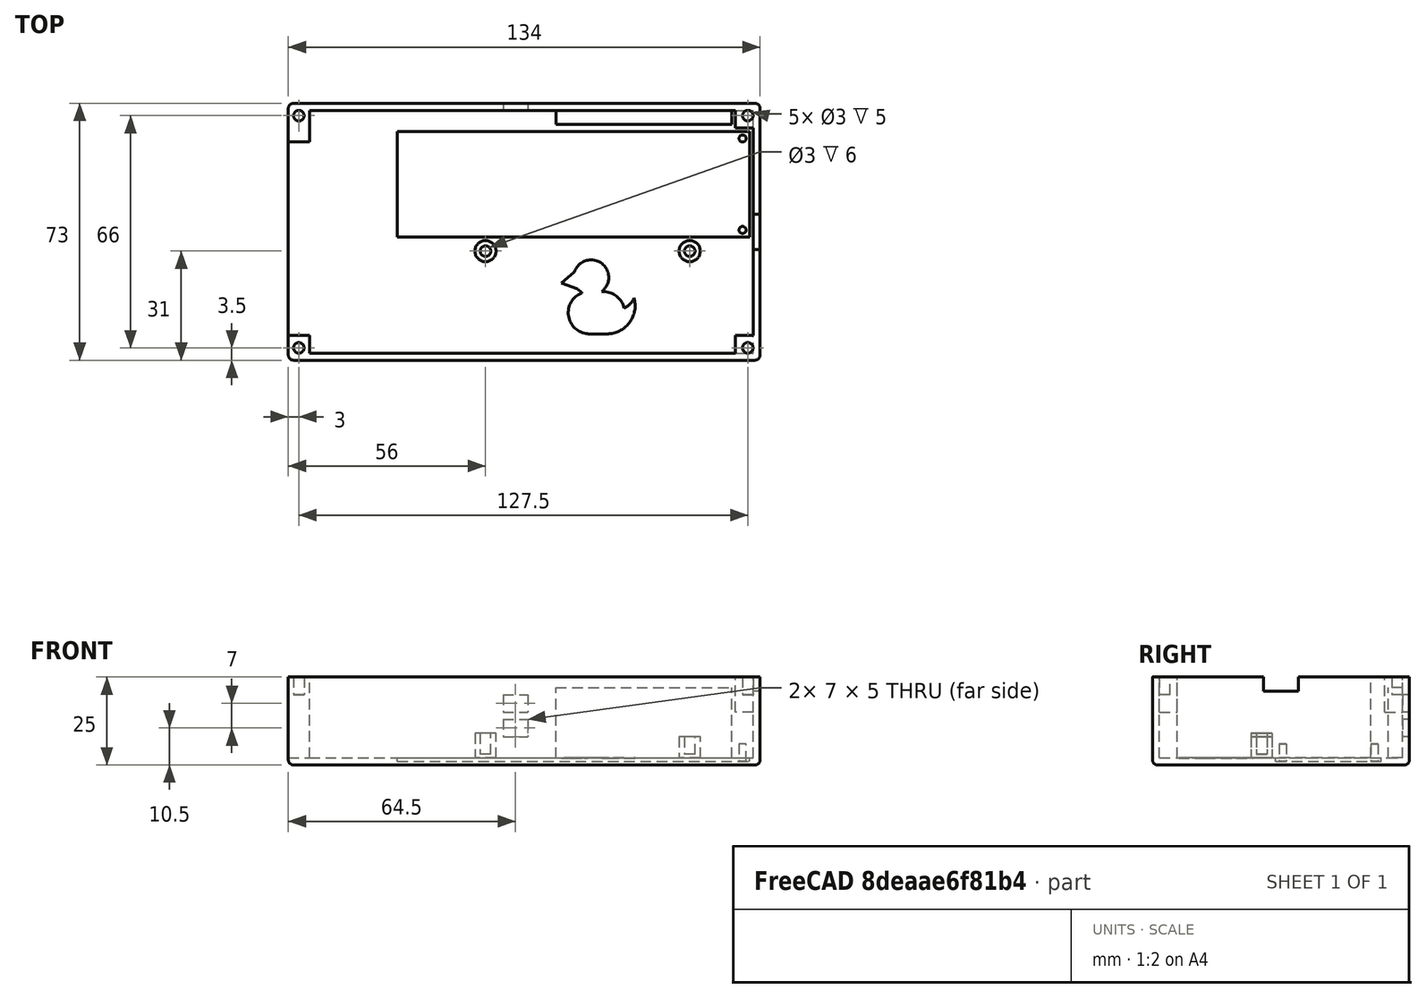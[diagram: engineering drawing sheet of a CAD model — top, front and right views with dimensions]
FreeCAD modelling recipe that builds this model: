
FCSTD DOCUMENT  (FreeCAD 1.0R39285 (Git))
Label: caseBottom
License: All rights reserved
LicenseURL: https://en.wikipedia.org/wiki/All_rights_reserved
objects: PartDesign::SubtractiveCylinder×12, PartDesign::SubtractiveBox×7, PartDesign::AdditiveCylinder×5, PartDesign::AdditiveBox×4, PartDesign::Fillet×4, PartDesign::SubtractivePrism×1, PartDesign::Body×1
note: 100 computed .brp shape members not serialized (recipe doc carries the construction recipe); baked Part::Feature solids carry a one-line shape summary decoded from their .brp

FEATURE [PartDesign::AdditiveBox] Box  label="base"
  AttacherType = Attacher::AttachEngine3D
  Height = 25
  Length = 134
  Refine = true
  Suppressed = false
  Width = 73
FEATURE [PartDesign::SubtractiveBox] Box001  label="primaryHollow"
  AttacherType = Attacher::AttachEngine3D
  AttachmentOffset = pos=(6,2,-23) rot=(0,0,1;0rad)
  AttachmentSupport = -> [Box]
  BaseFeature = -> Box
  Height = 23
  Length = 126
  MapMode = 5
  Placement = pos=(6,2,2) rot=(0,0,1;0rad)
  Refine = true
  Suppressed = false
  Width = 69
FEATURE [PartDesign::SubtractiveBox] Box002  label="dacGap"
  AttacherType = Attacher::AttachEngine3D
  AttachmentOffset = pos=(-8,5,0) rot=(0,0,1;0rad)
  AttachmentSupport = -> [Box001]
  BaseFeature = -> Box001
  Height = 23
  Length = 10
  MapMode = 2
  Placement = pos=(-2,7,2) rot=(0,0,1;0rad)
  Refine = true
  Suppressed = false
  Width = 55
FEATURE [PartDesign::SubtractiveBox] Box003  label="batteryPCBRecess"
  AttacherType = Attacher::AttachEngine3D
  AttachmentOffset = pos=(33,28,-1) rot=(0,0,1;0rad)
  AttachmentSupport = -> [Box002]
  BaseFeature = -> Box002
  Height = 1
  Length = 100
  MapMode = 5
  Placement = pos=(31,35,1) rot=(0,0,1;0rad)
  Refine = true
  Suppressed = false
  Width = 30
FEATURE [PartDesign::AdditiveCylinder] Cylinder  label="batteryPCBSupport1"
  Angle = 360
  AttacherType = Attacher::AttachEngine3D
  AttachmentOffset = pos=(98,2,0) rot=(0,0,1;0rad)
  AttachmentSupport = -> [Box003]
  BaseFeature = -> Box003
  FirstAngle = 0
  Height = 5
  MapMode = 5
  Placement = pos=(129,37,1) rot=(0,0,1;0rad)
  Radius = 1
  Refine = true
  SecondAngle = 0
  Suppressed = false
FEATURE [PartDesign::AdditiveCylinder] Cylinder001  label="batteryPCBSupport2"
  Angle = 360
  AttacherType = Attacher::AttachEngine3D
  AttachmentOffset = pos=(98,28,0) rot=(0,0,1;0rad)
  AttachmentSupport = -> [Box003]
  BaseFeature = -> Cylinder
  FirstAngle = 0
  Height = 5
  MapMode = 2
  Placement = pos=(129,63,1) rot=(0,0,1;0rad)
  Radius = 1
  Refine = true
  SecondAngle = 0
  Suppressed = false
FEATURE [PartDesign::AdditiveCylinder] Cylinder002  label="rpiSupport1"
  Angle = 360
  AttacherType = Attacher::AttachEngine3D
  AttachmentOffset = pos=(-15,-32,-1) rot=(0,0,1;0rad)
  AttachmentSupport = -> [Cylinder001]
  BaseFeature = -> Cylinder001
  FirstAngle = 0
  Height = 7
  MapMode = 5
  Placement = pos=(114,31,1) rot=(0,0,1;0rad)
  Radius = 3
  Refine = true
  SecondAngle = 0
  Suppressed = false
FEATURE [PartDesign::SubtractiveCylinder] Cylinder003  label="rpiSupport1Hollow"
  Angle = 360
  AttacherType = Attacher::AttachEngine3D
  AttachmentOffset = pos=(0,0,1) rot=(0,0,1;0rad)
  AttachmentSupport = -> [Cylinder002]
  BaseFeature = -> Cylinder002
  FirstAngle = 0
  Height = 6
  MapMode = 5
  Placement = pos=(114,31,3) rot=(0,0,1;0rad)
  Radius = 1.5
  Refine = true
  SecondAngle = 0
  Suppressed = false
FEATURE [PartDesign::AdditiveCylinder] Cylinder004  label="rpiSupport2"
  Angle = 360
  AttacherType = Attacher::AttachEngine3D
  AttachmentOffset = pos=(-58,0,0) rot=(0,0,1;0rad)
  AttachmentSupport = -> [Cylinder003]
  BaseFeature = -> Cylinder003
  FirstAngle = 0
  Height = 7
  MapMode = 5
  Placement = pos=(56,31,2) rot=(0,0,1;0rad)
  Radius = 3
  Refine = true
  SecondAngle = 0
  Suppressed = false
FEATURE [PartDesign::SubtractiveCylinder] Cylinder005  label="rpiSupport2Hollow"
  Angle = 360
  AttacherType = Attacher::AttachEngine3D
  AttachmentOffset = pos=(0,0,-6) rot=(0,0,1;0rad)
  AttachmentSupport = -> [Cylinder004]
  BaseFeature = -> Cylinder004
  FirstAngle = 0
  Height = 6
  MapMode = 5
  Placement = pos=(56,31,3) rot=(0,0,1;0rad)
  Radius = 1.5
  Refine = true
  SecondAngle = 0
  Suppressed = false
FEATURE [PartDesign::SubtractiveBox] Box004  label="powerSwitch"
  AttacherType = Attacher::AttachEngine3D
  AttachmentOffset = pos=(5,5,-3) rot=(0,0,1;0rad)
  AttachmentSupport = -> [Cylinder005]
  BaseFeature = -> Cylinder005
  Height = 7
  Length = 7
  MapMode = 5
  Placement = pos=(61,74,8) rot=(1,0,0;1.5708rad)
  Refine = true
  Suppressed = false
  Width = 5
FEATURE [PartDesign::SubtractiveBox] Box005  label="holdSwitch"
  AttacherType = Attacher::AttachEngine3D
  AttachmentOffset = pos=(0,7,-3) rot=(0,0,1;0rad)
  AttachmentSupport = -> [Box004]
  BaseFeature = -> Box004
  Height = 5
  Length = 7
  MapMode = 5
  Placement = pos=(61,74,15) rot=(1,0,0;1.5708rad)
  Refine = true
  Suppressed = false
  Width = 5
FEATURE [PartDesign::AdditiveBox] Box006  label="clickwheelSideSupport"
  AttacherType = Attacher::AttachEngine3D
  AttachmentOffset = pos=(15,-13,0) rot=(0,0,1;0rad)
  AttachmentSupport = -> [Box005]
  BaseFeature = -> Box005
  Height = 4
  Length = 50
  MapMode = 5
  Placement = pos=(76,71,2) rot=(1,0,0;1.5708rad)
  Refine = true
  Suppressed = false
  Width = 20
FEATURE [PartDesign::SubtractiveBox] Box007  label="usbPortHollow"
  AttacherType = Attacher::AttachEngine3D
  AttachmentOffset = pos=(-23,29.5,-2) rot=(0,0,1;0rad)
  AttachmentSupport = -> [Box006]
  BaseFeature = -> Box006
  Height = 2
  Length = 4
  MapMode = 5
  Placement = pos=(134,41.5,25) rot=(0.707107,0,-0.707107;3.14159rad)
  Refine = true
  Suppressed = false
  Width = 10
FEATURE [PartDesign::SubtractiveCylinder] Cylinder006  label="topScrewHollow1"
  Angle = 360
  AttacherType = Attacher::AttachEngine3D
  AttachmentOffset = pos=(-38,131,-5) rot=(0,0,1;0rad)
  AttachmentSupport = -> [Box007]
  BaseFeature = -> Box007
  FirstAngle = 0
  Height = 5
  MapMode = 5
  Placement = pos=(3,3.5,20) rot=(0,0,1;1.5708rad)
  Radius = 1.5
  Refine = true
  SecondAngle = 0
  Suppressed = false
FEATURE [PartDesign::SubtractiveCylinder] Cylinder007  label="topScrewHollow2"
  Angle = 360
  AttacherType = Attacher::AttachEngine3D
  AttachmentOffset = pos=(66,0,-5) rot=(0,0,1;0rad)
  AttachmentSupport = -> [Cylinder006]
  BaseFeature = -> Cylinder006
  FirstAngle = 0
  Height = 5
  MapMode = 5
  Placement = pos=(3,69.5,20) rot=(0,0,1;1.5708rad)
  Radius = 1.5
  Refine = true
  SecondAngle = 0
  Suppressed = false
FEATURE [PartDesign::AdditiveBox] Box008  label="bottomScrew1"
  AttacherType = Attacher::AttachEngine3D
  AttachmentOffset = pos=(-67.5,-129,-10) rot=(0,0,1;0rad)
  AttachmentSupport = -> [Cylinder007]
  BaseFeature = -> Cylinder007
  Height = 10
  Length = 5
  MapMode = 5
  Placement = pos=(132,2,15) rot=(0,0,1;1.5708rad)
  Refine = true
  Suppressed = false
  Width = 5
FEATURE [PartDesign::AdditiveBox] Box009  label="bottomScrew2"
  AttacherType = Attacher::AttachEngine3D
  AttachmentOffset = pos=(64,0,-10) rot=(0,0,1;0rad)
  AttachmentSupport = -> [Box008]
  BaseFeature = -> Box008
  Height = 10
  Length = 5
  MapMode = 5
  Placement = pos=(132,66,15) rot=(0,0,1;1.5708rad)
  Refine = true
  Suppressed = false
  Width = 5
FEATURE [PartDesign::SubtractiveCylinder] Cylinder008  label="bottomScrewHollow2"
  Angle = 360
  AttacherType = Attacher::AttachEngine3D
  AttachmentOffset = pos=(3.5,1.5,-5) rot=(0,0,1;0rad)
  AttachmentSupport = -> [Box009]
  BaseFeature = -> Box009
  FirstAngle = 0
  Height = 5
  MapMode = 5
  Placement = pos=(130.5,69.5,20) rot=(0,0,1;1.5708rad)
  Radius = 1.5
  Refine = true
  SecondAngle = 0
  Suppressed = false
FEATURE [PartDesign::SubtractiveCylinder] Cylinder009  label="BottomScrewHollow1"
  Angle = 360
  AttacherType = Attacher::AttachEngine3D
  AttachmentOffset = pos=(-66,0,-5) rot=(0,0,1;0rad)
  AttachmentSupport = -> [Cylinder008]
  BaseFeature = -> Cylinder008
  FirstAngle = 0
  Height = 5
  MapMode = 5
  Placement = pos=(130.5,3.5,20) rot=(0,0,1;1.5708rad)
  Radius = 1.5
  Refine = true
  SecondAngle = 0
  Suppressed = false
FEATURE [PartDesign::Fillet] Fillet
  Base = -> Cylinder009 [Edge62]
  BaseFeature = -> Cylinder009
  Placement = pos=(130.5,3.5,20) rot=(0,0,1;1.5708rad)
  Radius = 1.5
  Refine = true
  SupportTransform = false
  Suppressed = false
  UseAllEdges = false
FEATURE [PartDesign::Fillet] Fillet001
  Base = -> Fillet [Edge14]
  BaseFeature = -> Fillet
  Placement = pos=(130.5,3.5,20) rot=(0,0,1;1.5708rad)
  Radius = 1.5
  Refine = true
  SupportTransform = false
  Suppressed = false
  UseAllEdges = false
FEATURE [PartDesign::Fillet] Fillet002
  Base = -> Fillet001 [Edge31]
  BaseFeature = -> Fillet001
  Placement = pos=(130.5,3.5,20) rot=(0,0,1;1.5708rad)
  Radius = 1.5
  Refine = true
  SupportTransform = false
  Suppressed = false
  UseAllEdges = false
FEATURE [PartDesign::Fillet] Fillet003
  Base = -> Fillet002 [Edge1]
  BaseFeature = -> Fillet002
  Placement = pos=(130.5,3.5,20) rot=(0,0,1;1.5708rad)
  Radius = 1.5
  Refine = true
  SupportTransform = false
  Suppressed = false
  UseAllEdges = false
FEATURE [PartDesign::SubtractiveCylinder] Cylinder010
  Angle = 360
  AttacherType = Attacher::AttachEngine3D
  AttachmentOffset = pos=(10,40,-0.1) rot=(0,0,1;0rad)
  AttachmentSupport = -> [Fillet003]
  BaseFeature = -> Fillet003
  FirstAngle = 0
  Height = 0.1
  MapMode = 5
  Placement = pos=(90.5,13.5,1.9) rot=(0,0,1;1.5708rad)
  Radius = 6
  Refine = true
  SecondAngle = 0
  Suppressed = false
FEATURE [PartDesign::SubtractiveCylinder] Cylinder011
  Angle = 360
  AttacherType = Attacher::AttachEngine3D
  AttachmentOffset = pos=(0,5,-0.1) rot=(0,0,1;0rad)
  AttachmentSupport = -> [Cylinder010]
  BaseFeature = -> Cylinder010
  FirstAngle = 0
  Height = 0.1
  MapMode = 5
  Placement = pos=(85.5,13.5,1.9) rot=(0,0,1;1.5708rad)
  Radius = 6
  Refine = true
  SecondAngle = 0
  Suppressed = false
FEATURE [PartDesign::SubtractiveBox] Box010
  AttacherType = Attacher::AttachEngine3D
  AttachmentOffset = pos=(-6,-5.5,-0.1) rot=(0,0,1;0rad)
  AttachmentSupport = -> [Cylinder011]
  BaseFeature = -> Cylinder011
  Height = 0.1
  Length = 12
  MapMode = 5
  Placement = pos=(91,7.5,1.9) rot=(0,0,1;1.5708rad)
  Refine = true
  Suppressed = false
  Width = 6
FEATURE [PartDesign::SubtractiveCylinder] Cylinder012
  Angle = 360
  AttacherType = Attacher::AttachEngine3D
  AttachmentOffset = pos=(16,5,-0.1) rot=(0,0,1;0rad)
  AttachmentSupport = -> [Box010]
  BaseFeature = -> Box010
  FirstAngle = 0
  Height = 0.1
  MapMode = 5
  Placement = pos=(86,23.5,1.9) rot=(0,0,1;1.5708rad)
  Radius = 5
  Refine = true
  SecondAngle = 0
  Suppressed = false
FEATURE [PartDesign::SubtractiveCylinder] Cylinder013
  Angle = 360
  AttacherType = Attacher::AttachEngine3D
  AttachmentOffset = pos=(-8,-4.5,-0.1) rot=(0,0,1;0rad)
  AttachmentSupport = -> [Cylinder012]
  BaseFeature = -> Cylinder012
  FirstAngle = 0
  Height = 0.1
  MapMode = 5
  Placement = pos=(90.5,15.5,1.9) rot=(0,0,1;1.5708rad)
  Radius = 8
  Refine = true
  SecondAngle = 0
  Suppressed = false
FEATURE [PartDesign::AdditiveCylinder] Cylinder014
  Angle = 360
  AttacherType = Attacher::AttachEngine3D
  AttachmentOffset = pos=(4,-3,-0.1) rot=(0,0,1;0rad)
  AttachmentSupport = -> [Cylinder013]
  BaseFeature = -> Cylinder013
  FirstAngle = 0
  Height = 0.1
  MapMode = 5
  Placement = pos=(93.5,19.5,1.9) rot=(0,0,1;1.5708rad)
  Radius = 5
  Refine = true
  SecondAngle = 0
  Suppressed = false
FEATURE [PartDesign::SubtractiveCylinder] Cylinder015
  Angle = 360
  AttacherType = Attacher::AttachEngine3D
  AttachmentOffset = pos=(-6,4,-0.1) rot=(0,0,1;0rad)
  AttachmentSupport = -> [Cylinder014]
  BaseFeature = -> Cylinder014
  FirstAngle = 0
  Height = 0.1
  MapMode = 5
  Placement = pos=(89.5,13.5,1.9) rot=(0,0,1;1.5708rad)
  Radius = 6
  Refine = true
  SecondAngle = 0
  Suppressed = false
FEATURE [PartDesign::SubtractiveCylinder] Cylinder016
  Angle = 360
  AttacherType = Attacher::AttachEngine3D
  AttachmentOffset = pos=(10,3.5,-0.1) rot=(0,0,1;0rad)
  AttachmentSupport = -> [Cylinder015]
  BaseFeature = -> Cylinder015
  FirstAngle = 0
  Height = 0.1
  MapMode = 5
  Placement = pos=(86,23.5,1.9) rot=(0,0,1;1.5708rad)
  Radius = 5
  Refine = true
  SecondAngle = 0
  Suppressed = false
FEATURE [PartDesign::SubtractivePrism] Prism
  AttacherType = Attacher::AttachEngine3D
  AttachmentOffset = pos=(-1,5.5,-0.1) rot=(0,0,-1;0.349066rad)
  AttachmentSupport = -> [Cylinder016]
  BaseFeature = -> Cylinder016
  Circumradius = 3
  FirstAngle = 0
  Height = 0.1
  MapMode = 5
  Placement = pos=(80.5,22.5,1.9) rot=(0,0,1;1.22173rad)
  Polygon = 3
  Refine = true
  SecondAngle = 0
  Suppressed = false
FEATURE [PartDesign::Body] Body
  AllowCompound = false
  Group = -> [Box,Box001,Box002,Box003,Cylinder,Cylinder001,Cylinder002,Cylinder003,Cylinder004,Cylinder005,Box004,Box005,Box006,Box007,Cylinder006,Cylinder007,Box008,Box009,Cylinder008,Cylinder009,Fillet,Fillet001,Fillet002,Fillet003,Cylinder010,Cylinder011,Box010,Cylinder012,Cylinder013,Cylinder014,Cylinder015,Cylinder016,Prism]
  Origin = -> Origin
  Tip = -> Prism
